# Revit family: PRD_FrankeWS_TltBrshHldrs_ToiletBrushHolder_BS686
name_source: partatom
category: Specialty Equipment
revit_build: Autodesk Revit 2018 (Build: 20190510_1515(x64)
units: mm (PartAtom-declared; Revit-internal decimal feet)

## family parameters
Cut with Voids When Loaded = No
Host = Face
OmniClass Number = 23.40.00.00
OmniClass Title = Equipment and Furnishings
Part Type = Normal
Room Calculation Point = No
Round Connector Dimension = Use Diameter
Shared = No

## types (1)
- BS686
    AssetType = Fixed
    BIMObjectName = PRD_AR_ToiletBrushHolders_ToiletBrushHolder_BS686
    BrushMaterial = PRD_AR_ToiletBrush
    Category = Pr_40_20_76_86, Toilet brush holders
    Color = Stainless steel
    Constituents = White nylon brush with flushing rim cleaner
    Default Elevation = 100 mm  [stored 0.328084 ft]
    Description = Toilet brush holder for wall mounting, stainless steel, surface satin finished, material thickness 0.9 mm, white nylon brush with flushing rim cleaner, integrated drip tray, brush has to be hooked in, incl. stainless steel screws and dowels.
    DurationUnit = year
    Features = stainless steel, 0.90 mm, satin finished, wall mounting, 135x235x135 mm (WxHxD)
    Finish = Satin finished
    FinishAndColour = Stainless steel, satin finished
    Form = Wall mounted
    IfcExportAs = IfcFurnitureType
    IfcExportType = NOTDEFINED
    IntegralAccessories = White nylon brush with flushing rim cleaner. Stainless steel screws and dowels incl.
    MainColor = Stainless steel
    Manufacturer = KWC Group AG
    ManufacturerName = KWC Group AG
    ManufacturerURL = www.kwc.com
    Material = Stainless steel
    Model = BS686
    ModelNumber = 2000057078
    ModelReference = BS686
    NBSDescription = Toilet brush holders
    NBSReference = 45-35-72/364
    Name = Toilet brush holder BS686
    NominalDepth = 135 mm  [stored 0.442913 ft]
    NominalHeight = 235 mm  [stored 0.770997 ft]
    NominalLength = 135 mm  [stored 0.442913 ft]
    NominalWidth = 135 mm  [stored 0.442913 ft]
    ProductInformation = https://pim.kwc.com
    Size = 135 x 235 x 135 mm
    Style = Toilet brush holder
    ToiletBrushHolderMaterial = PRD_AR_StainlessSteel_SatinFinished
    URL = www.kwc.com
    Uniclass2015Code = Pr_40_20_76_86
    Uniclass2015Title = Toilet brush holders
    Uniclass2015Version = Products v1.5
    Version = 1
    WarrantyDurationUnit = year

note: [stored X ft] marks values corroborated as IEEE doubles in the binary element streams (Revit-internal decimal feet)

## geometry (parser evidence)
native form markers: Sweep x2
no freeform markers — native parametric forms only
